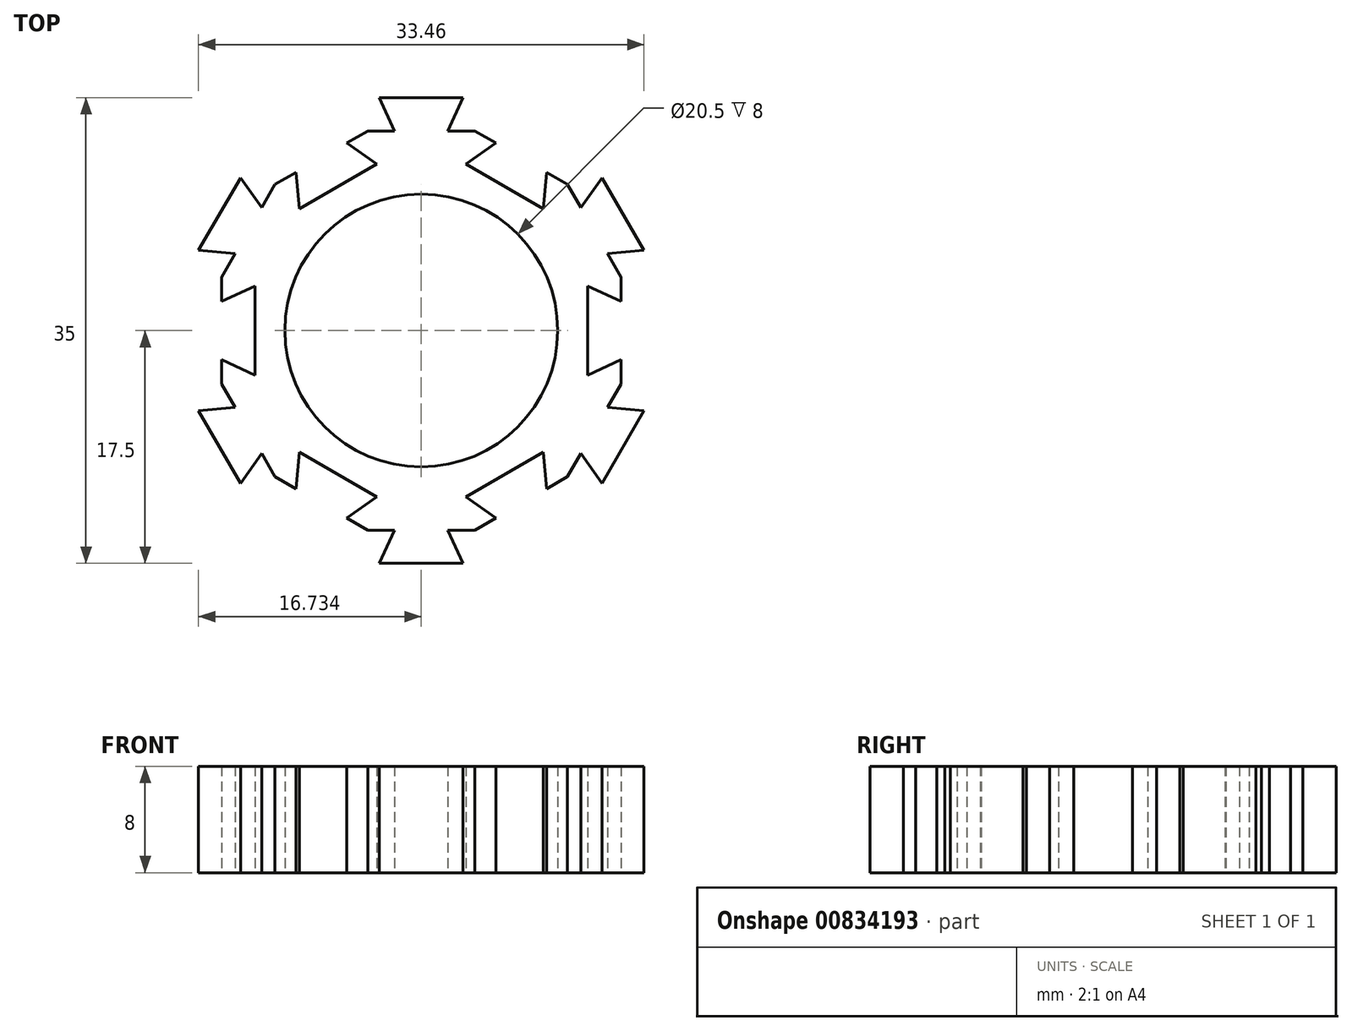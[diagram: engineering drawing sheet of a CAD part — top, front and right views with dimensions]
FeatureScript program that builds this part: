
annotation { "Feature Type Name" : "Feature", "Feature Type Description" : "" }
export const myFeature = defineFeature(function(context is Context, id is Id, definition is map)
    precondition{}
    {
        {
            var Q0;
            Q0=qCreatedBy(makeId("Top.planeOp"),FACE);
            var sketch = newSketch(context, id + "F0", { "sketchPlane" : qUnion([Q0])});
            skCircle(sketch, "E0", {"center": v(54.4, 0) * mm, "radius": 10.25 * mm});
            skLineSegment(sketch, "E1.1", {"start": v(57.74, 12.5) * mm, "end": v(63.54, 9.15) * mm});
            skLineSegment(sketch, "E1.3", {"start": v(66.9, 3.35) * mm, "end": v(66.9, -3.35) * mm});
            skLineSegment(sketch, "E1.5", {"start": v(63.54, -9.15) * mm, "end": v(57.74, -12.5) * mm});
            skLineSegment(sketch, "E1.7", {"start": v(51.04, -12.5) * mm, "end": v(45.24, -9.15) * mm});
            skLineSegment(sketch, "E1.9", {"start": v(41.9, -3.35) * mm, "end": v(41.9, 3.35) * mm});
            skLineSegment(sketch, "E1.11", {"start": v(45.24, 9.15) * mm, "end": v(51.04, 12.5) * mm});
            skPoint(sketch, "E1.0.midPoint", {"position": v(54.4, 12.5) * mm});
            skLineSegment(sketch, "E2.0", {"start": v(50.38, 15) * mm, "end": v(52.4, 15) * mm});
            skLineSegment(sketch, "E2.1", {"start": v(58.41, 15) * mm, "end": v(59.99, 14.1) * mm});
            skLineSegment(sketch, "E2.2", {"start": v(65.38, 10.98) * mm, "end": v(66.38, 9.23) * mm});
            skLineSegment(sketch, "E2.3", {"start": v(69.4, 4.02) * mm, "end": v(69.4, 2.2) * mm});
            skLineSegment(sketch, "E2.4", {"start": v(69.4, -4.02) * mm, "end": v(68.38, -5.77) * mm});
            skLineSegment(sketch, "E2.5", {"start": v(65.38, -10.98) * mm, "end": v(63.8, -11.9) * mm});
            skLineSegment(sketch, "E2.6", {"start": v(58.41, -15) * mm, "end": v(56.4, -15) * mm});
            skLineSegment(sketch, "E2.7", {"start": v(50.38, -15) * mm, "end": v(48.8, -14.1) * mm});
            skLineSegment(sketch, "E2.8", {"start": v(43.41, -10.98) * mm, "end": v(42.4, -9.23) * mm});
            skLineSegment(sketch, "E2.9", {"start": v(39.4, -4.02) * mm, "end": v(39.4, -2.2) * mm});
            skLineSegment(sketch, "E2.10", {"start": v(39.4, 4.02) * mm, "end": v(40.4, 5.77) * mm});
            skLineSegment(sketch, "E2.11", {"start": v(43.41, 10.98) * mm, "end": v(44.99, 11.9) * mm});
            skPoint(sketch, "E2.0.midPoint", {"position": v(54.4, 15) * mm});
            skLineSegment(sketch, "E3.1.0", {"start": v(48.8, 14.1) * mm, "end": v(51.04, 12.5) * mm});
            skLineSegment(sketch, "E3.1.1", {"start": v(44.99, 11.9) * mm, "end": v(45.24, 9.15) * mm});
            skLineSegment(sketch, "E3.3.0", {"start": v(39.4, 2.2) * mm, "end": v(41.9, 3.35) * mm});
            skLineSegment(sketch, "E3.3.1", {"start": v(39.4, -2.2) * mm, "end": v(41.9, -3.35) * mm});
            skLineSegment(sketch, "E3.5.0", {"start": v(44.99, -11.9) * mm, "end": v(45.24, -9.15) * mm});
            skLineSegment(sketch, "E3.5.1", {"start": v(48.8, -14.1) * mm, "end": v(51.04, -12.5) * mm});
            skLineSegment(sketch, "E3.7.0", {"start": v(59.99, -14.1) * mm, "end": v(57.74, -12.5) * mm});
            skLineSegment(sketch, "E3.7.1", {"start": v(63.8, -11.9) * mm, "end": v(63.54, -9.15) * mm});
            skLineSegment(sketch, "E3.9.0", {"start": v(69.4, -2.2) * mm, "end": v(66.9, -3.35) * mm});
            skLineSegment(sketch, "E3.9.1", {"start": v(69.4, 2.2) * mm, "end": v(66.9, 3.35) * mm});
            skLineSegment(sketch, "E3.11.0", {"start": v(63.8, 11.9) * mm, "end": v(63.54, 9.15) * mm});
            skLineSegment(sketch, "E3.11.1", {"start": v(59.99, 14.1) * mm, "end": v(57.74, 12.5) * mm});
            skLineSegment(sketch, "E4", {"start": v(57.74, 15) * mm, "end": v(57.54, 15) * mm});
            skLineSegment(sketch, "E5", {"start": v(57.54, 17.5) * mm, "end": v(56.4, 15) * mm});
            skLineSegment(sketch, "E6.MirrorCS", {"start": v(51.24, 17.5) * mm, "end": v(52.4, 15) * mm});
            skLineSegment(sketch, "E7", {"start": v(51.24, 17.5) * mm, "end": v(57.54, 17.5) * mm});
            skLineSegment(sketch, "E8.1.0", {"start": v(37.66, 6.02) * mm, "end": v(40.4, 5.77) * mm});
            skLineSegment(sketch, "E8.1.1", {"start": v(37.66, 6.02) * mm, "end": v(40.81, 11.48) * mm});
            skLineSegment(sketch, "E8.1.2", {"start": v(40.81, 11.48) * mm, "end": v(42.4, 9.23) * mm});
            skLineSegment(sketch, "E8.2.0", {"start": v(40.81, -11.48) * mm, "end": v(42.4, -9.23) * mm});
            skLineSegment(sketch, "E8.2.1", {"start": v(40.81, -11.48) * mm, "end": v(37.66, -6.02) * mm});
            skLineSegment(sketch, "E8.2.2", {"start": v(37.66, -6.02) * mm, "end": v(40.4, -5.77) * mm});
            skLineSegment(sketch, "E8.3.0", {"start": v(57.54, -17.5) * mm, "end": v(56.4, -15) * mm});
            skLineSegment(sketch, "E8.3.1", {"start": v(57.54, -17.5) * mm, "end": v(51.24, -17.5) * mm});
            skLineSegment(sketch, "E8.3.2", {"start": v(51.24, -17.5) * mm, "end": v(52.4, -15) * mm});
            skLineSegment(sketch, "E8.4.0", {"start": v(71.12, -6.02) * mm, "end": v(68.38, -5.77) * mm});
            skLineSegment(sketch, "E8.4.1", {"start": v(71.12, -6.02) * mm, "end": v(67.98, -11.48) * mm});
            skLineSegment(sketch, "E8.4.2", {"start": v(67.98, -11.48) * mm, "end": v(66.38, -9.23) * mm});
            skLineSegment(sketch, "E8.5.0", {"start": v(67.97, 11.48) * mm, "end": v(66.38, 9.23) * mm});
            skLineSegment(sketch, "E8.5.1", {"start": v(67.97, 11.48) * mm, "end": v(71.12, 6.02) * mm});
            skLineSegment(sketch, "E8.5.2", {"start": v(71.12, 6.02) * mm, "end": v(68.38, 5.77) * mm});
            skLineSegment(sketch, "E9.trimOffspring", {"start": v(48.8, 14.1) * mm, "end": v(50.38, 15) * mm});
            skLineSegment(sketch, "E10.trimOffspring", {"start": v(56.4, 15) * mm, "end": v(58.41, 15) * mm});
            skLineSegment(sketch, "E11.trimOffspring", {"start": v(63.8, 11.9) * mm, "end": v(65.38, 10.98) * mm});
            skLineSegment(sketch, "E12.trimOffspring", {"start": v(42.4, 9.23) * mm, "end": v(43.41, 10.98) * mm});
            skLineSegment(sketch, "E13.trimOffspring", {"start": v(39.4, 2.2) * mm, "end": v(39.4, 4.02) * mm});
            skLineSegment(sketch, "E14.trimOffspring", {"start": v(40.4, -5.77) * mm, "end": v(39.4, -4.02) * mm});
            skLineSegment(sketch, "E15.trimOffspring", {"start": v(44.99, -11.9) * mm, "end": v(43.41, -10.98) * mm});
            skLineSegment(sketch, "E16.trimOffspring", {"start": v(52.4, -15) * mm, "end": v(50.38, -15) * mm});
            skLineSegment(sketch, "E17.trimOffspring", {"start": v(59.99, -14.1) * mm, "end": v(58.41, -15) * mm});
            skLineSegment(sketch, "E18.trimOffspring", {"start": v(69.4, -2.2) * mm, "end": v(69.4, -4.02) * mm});
            skLineSegment(sketch, "E19.trimOffspring", {"start": v(68.38, 5.77) * mm, "end": v(69.4, 4.02) * mm});
            skLineSegment(sketch, "E20.trimOffspring", {"start": v(66.38, -9.23) * mm, "end": v(65.38, -10.98) * mm});
            skSolve(sketch);
        }
        {
            var Q0;
            Q0=makeQuery(id+"F0.imprint","IMPRINT",FACE,{"disambiguationData":[TD([[makeQuery(id+"F0.imprint","IMPRINT",EDGE,{"derivedFrom":sQuery(id+"F0.wireOp",EDGE,"E0")}),-1.0]])]});
            extrude(context, id + "F1", {"entities" : qUnion([Q0]), "depth" : 8 * mm, "offsetDistance" : 25 * mm});
        }
    });
